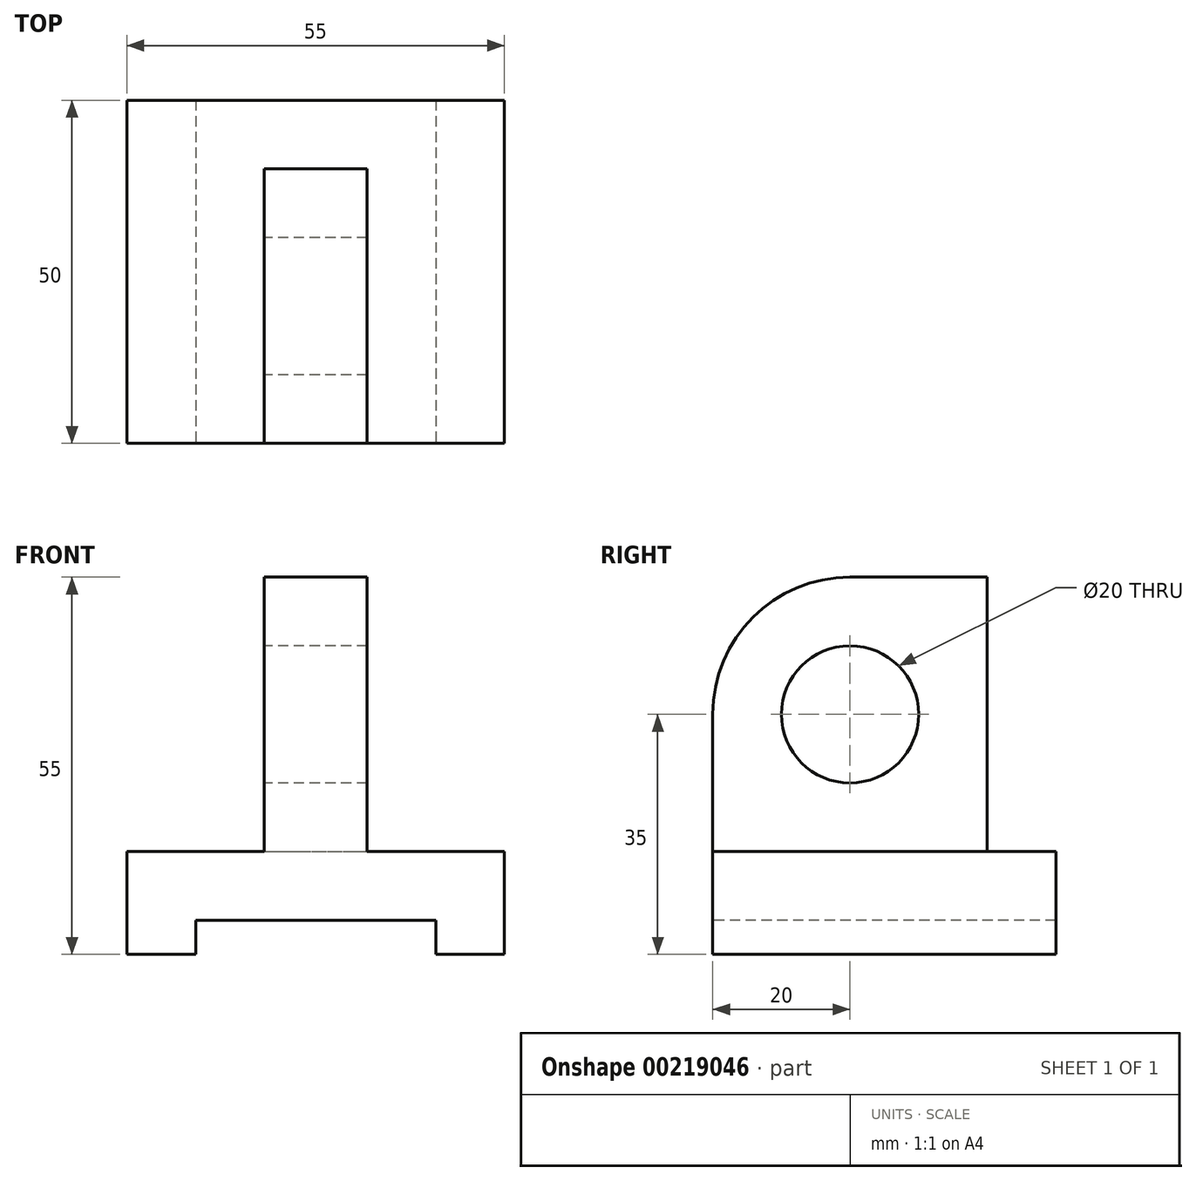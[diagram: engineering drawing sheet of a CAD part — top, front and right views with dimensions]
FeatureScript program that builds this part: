
annotation { "Feature Type Name" : "Feature", "Feature Type Description" : "" }
export const myFeature = defineFeature(function(context is Context, id is Id, definition is map)
    precondition{}
    {
        {
            var Q0;
            Q0=qCreatedBy(makeId("Front.planeOp"),FACE);
            var sketch = newSketch(context, id + "F0", { "sketchPlane" : qUnion([Q0])});
            skLineSegment(sketch, "E0", {"start": v(0, 0) * mm, "end": v(10, 0) * mm});
            skLineSegment(sketch, "E1", {"start": v(55, 0) * mm, "end": v(55, 15) * mm});
            skLineSegment(sketch, "E2", {"start": v(55, 15) * mm, "end": v(35, 15) * mm});
            skLineSegment(sketch, "E3", {"start": v(35, 15) * mm, "end": v(35, 55) * mm});
            skLineSegment(sketch, "E4", {"start": v(35, 55) * mm, "end": v(20, 55) * mm});
            skLineSegment(sketch, "E5", {"start": v(20, 55) * mm, "end": v(20, 15) * mm});
            skLineSegment(sketch, "E6", {"start": v(20, 15) * mm, "end": v(0, 15) * mm});
            skLineSegment(sketch, "E7", {"start": v(0, 15) * mm, "end": v(0, 0) * mm});
            skLineSegment(sketch, "E8", {"start": v(10, 0) * mm, "end": v(10, 5) * mm});
            skLineSegment(sketch, "E9", {"start": v(10, 5) * mm, "end": v(45, 5) * mm});
            skLineSegment(sketch, "E10", {"start": v(45, 5) * mm, "end": v(45, 0) * mm});
            skLineSegment(sketch, "E11", {"start": v(20, 15) * mm, "end": v(35, 15) * mm});
            skLineSegment(sketch, "E12.trimOffspring", {"start": v(45, 0) * mm, "end": v(55, 0) * mm});
            skSolve(sketch);
        }
        {
            var Q0;
            Q0=makeQuery(id+"F0.imprint","IMPRINT",FACE,{"disambiguationData":[TD([[makeQuery(id+"F0.imprint","IMPRINT",EDGE,{"derivedFrom":sQuery(id+"F0.wireOp",EDGE,"E0")}),1.0]])]});
            extrude(context, id + "F1", {"entities" : qUnion([Q0]), "oppositeDirection" : true, "depth" : 50 * mm});
        }
        {
            var Q0;
            Q0=makeQuery(id+"F0.imprint","IMPRINT",FACE,{"disambiguationData":[TD([[makeQuery(id+"F0.imprint","IMPRINT",EDGE,{"derivedFrom":sQuery(id+"F0.wireOp",EDGE,"E3")}),1.0]])]});
            extrude(context, id + "F2", {"entities" : qUnion([Q0]), "operationType" : NewBodyOperationType.ADD, "oppositeDirection" : true, "depth" : 40 * mm});
        }
        {
            var Q0;
            Q0=makeQuery(id+"F2.opExtrude","SWEPT_FACE",FACE,{"disambiguationData":[OSD([sQuery(id+"F0.wireOp",EDGE,"E5")])]});
            var sketch = newSketch(context, id + "F3", { "sketchPlane" : qUnion([Q0])});
            skCircle(sketch, "E13", {"center": v(-20, 35) * mm, "radius": 10 * mm});
            skArc(sketch, "E14", {"start": v(0, 35) * mm, "mid": v(-5.86, 49.14) * mm, "end": v(-20, 55) * mm});
            skLineSegment(sketch, "E15.0", {"start": v(-20, 55) * mm, "end": v(0, 55) * mm});
            skLineSegment(sketch, "E16.0", {"start": v(0, 55) * mm, "end": v(0, 35) * mm});
            skPoint(sketch, "E17.orphan", {"position": v(0, 15) * mm});
            skPoint(sketch, "E18.0.start.orphan", {"position": v(-50, 15) * mm});
            skPoint(sketch, "E19.0.end.orphan", {"position": v(-40, 15) * mm});
            skPoint(sketch, "E20.orphan", {"position": v(-40, 55) * mm});
            skSolve(sketch);
        }
        {
            var Q0;
            Q0=makeQuery(id+"F3.imprint","IMPRINT",FACE,{"disambiguationData":[TD([[makeQuery(id+"F3.imprint","IMPRINT",EDGE,{"derivedFrom":sQuery(id+"F3.wireOp",EDGE,"E13")}),1.0]])]});
            var Q1;
            Q1=makeQuery(id+"F2.opExtrude","SWEPT_FACE",FACE,{"disambiguationData":[OSD([sQuery(id+"F0.wireOp",EDGE,"E3")])]});
            extrude(context, id + "F4", {"entities" : qUnion([Q0]), "operationType" : NewBodyOperationType.REMOVE, "endBound" : BoundingType.UP_TO_SURFACE, "oppositeDirection" : true, "endBoundEntityFace" : qUnion([Q1]), "depth" : 25 * mm});
        }
        {
            var Q0;
            Q0=makeQuery(id+"F3.imprint","IMPRINT",FACE,{"disambiguationData":[TD([[makeQuery(id+"F3.imprint","IMPRINT",EDGE,{"derivedFrom":sQuery(id+"F3.wireOp",EDGE,"E14")}),-1.0]])]});
            extrude(context, id + "F5", {"entities" : qUnion([Q0]), "operationType" : NewBodyOperationType.REMOVE, "endBound" : BoundingType.UP_TO_NEXT, "oppositeDirection" : true, "depth" : 25 * mm});
        }
    });
